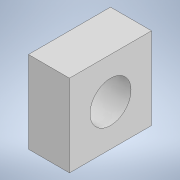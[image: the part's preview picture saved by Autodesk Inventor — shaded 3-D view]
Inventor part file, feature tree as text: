
AUTODESK INVENTOR PART (.ipt)
format: ipt  version: 2022 (Build 260153000, 153)  size: 94,208 bytes
history: native  units: mm
features: extrude x1, sketch x1
ambient origin geometry x8: Origin, YZ Plane, XZ Plane, XY Plane, X Axis, Y Axis, Z Axis, Center Point
bodies: Solid1 (feature_tree)
feature tree (2):
  extrude  "Extrusion1"  Depth=10.0mm
  sketch  "Sketch1"  dims[d0=10.0mm d1=10.0mm d2=5.0mm d3=5.0mm d4=0.0mm]
